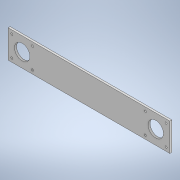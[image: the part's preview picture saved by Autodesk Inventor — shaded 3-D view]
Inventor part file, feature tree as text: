
AUTODESK INVENTOR PART (.ipt)
format: ipt  version: 2021 (Build 250183000, 183)  size: 122,368 bytes
history: native  units: mm
features: sketch x2, hole x2, other x1, extrude x1, mirror x1
ambient origin geometry x8: Origin, YZ Plane, XZ Plane, XY Plane, X Axis, Y Axis, Z Axis, Center Point
bodies: Body1 (feature_tree)
feature tree (7):
  other  "Sólido1"
  extrude  "Extrusão1"  Depth=42.0mm
  sketch  "Esboço2"  dims[d2=3.0mm d3=0.0mm d4=42.0mm d5=42.0mm d6=31.0mm d7=31.0mm d8=3.0mm d9=6.0mm d10=4.0mm d11=2.0mm d12=90.0deg d13=8.0mm d14=20.594885mm d15=23.0mm d16=6.0mm d17=4.0mm d18=2.0mm d19=90.0deg d20=8.0mm d21=20.594885mm]
  hole  "Furo1"  [1 undecoded]
  hole  "Furo2"  [1 undecoded]
  mirror  "Espelhamento1"
  sketch  "Esboço1"  dims[d0=242.0mm d1=42.0mm]
note: 2 required parameter values undecoded (feature->parameter linkage not recoverable at this tier; creation-order binding heuristic only, values carry confidence <= 0.55)
